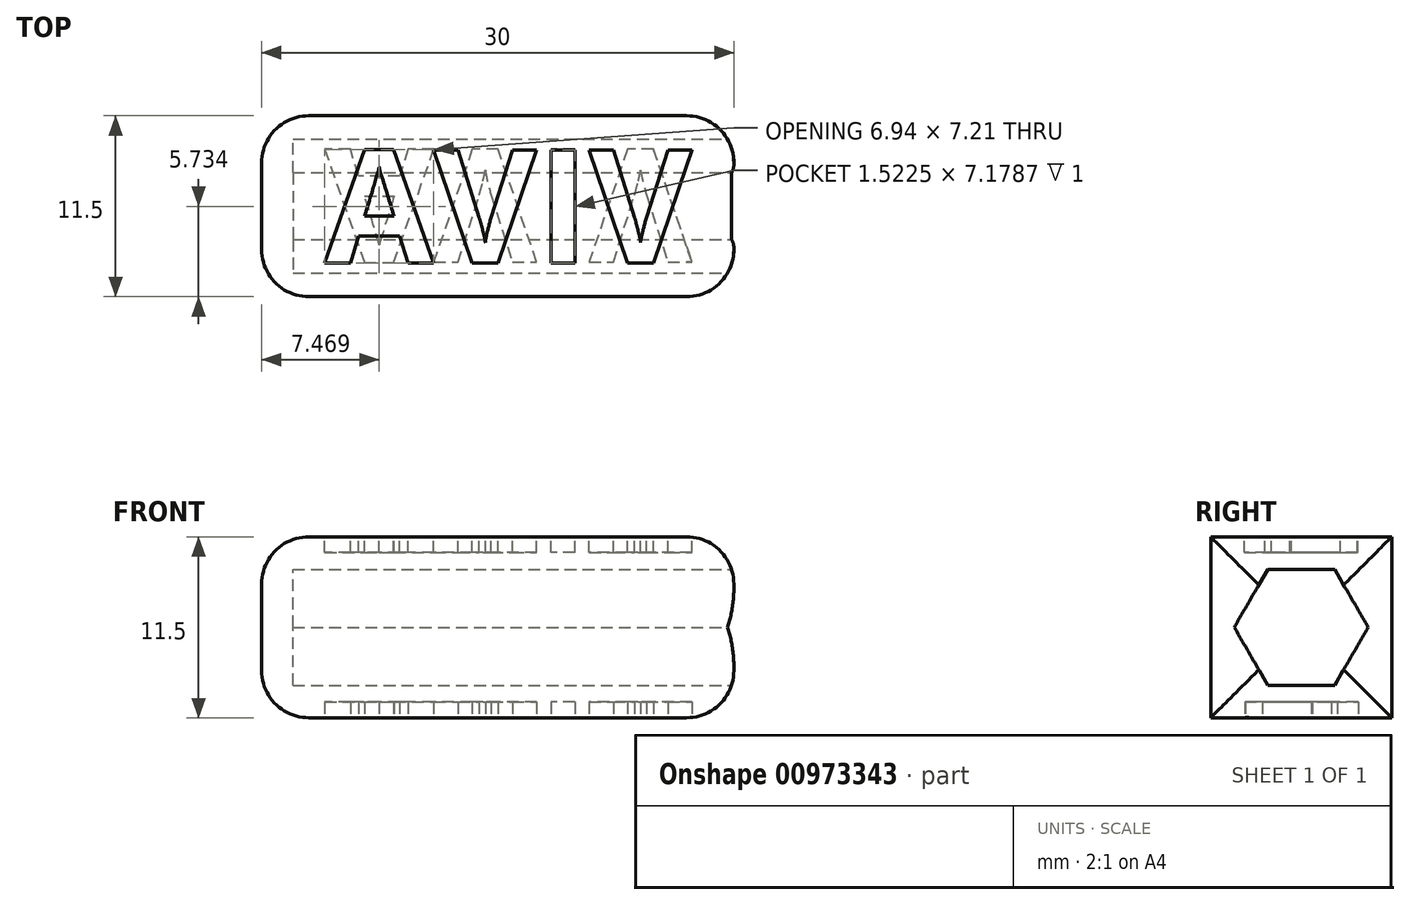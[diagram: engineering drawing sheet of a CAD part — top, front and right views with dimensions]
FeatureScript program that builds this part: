
annotation { "Feature Type Name" : "Feature", "Feature Type Description" : "" }
export const myFeature = defineFeature(function(context is Context, id is Id, definition is map)
    precondition{}
    {
        {
            var Q0;
            Q0=qCreatedBy(makeId("Top.planeOp"),FACE);
            var sketch = newSketch(context, id + "F0", { "sketchPlane" : qUnion([Q0])});
            skCircle(sketch, "E0.cCircle", {"center": v(0, 0) * mm, "radius": 4.25 * mm, "construction": true});
            skLineSegment(sketch, "E0.0", {"start": v(0, 4.25) * mm, "end": v(3.68, 2.13) * mm});
            skLineSegment(sketch, "E0.1", {"start": v(3.68, 2.13) * mm, "end": v(3.68, -2.12) * mm});
            skLineSegment(sketch, "E0.2", {"start": v(3.68, -2.12) * mm, "end": v(0, -4.25) * mm});
            skLineSegment(sketch, "E0.3", {"start": v(0, -4.25) * mm, "end": v(-3.68, -2.13) * mm});
            skLineSegment(sketch, "E0.4", {"start": v(-3.68, -2.13) * mm, "end": v(-3.68, 2.12) * mm});
            skLineSegment(sketch, "E0.5", {"start": v(-3.68, 2.12) * mm, "end": v(0, 4.25) * mm});
            skLineSegment(sketch, "E1.bottom", {"start": v(5.75, 5.75) * mm, "end": v(-5.75, 5.75) * mm});
            skLineSegment(sketch, "E1.top", {"start": v(5.75, -5.75) * mm, "end": v(-5.75, -5.75) * mm});
            skLineSegment(sketch, "E1.left", {"start": v(5.75, 5.75) * mm, "end": v(5.75, -5.75) * mm});
            skLineSegment(sketch, "E1.right", {"start": v(-5.75, 5.75) * mm, "end": v(-5.75, -5.75) * mm});
            skSolve(sketch);
        }
        {
            var Q0;
            Q0=makeQuery(id+"F0.imprint","IMPRINT",FACE,{"disambiguationData":[TD([[makeQuery(id+"F0.imprint","IMPRINT",EDGE,{"derivedFrom":sQuery(id+"F0.wireOp",EDGE,"E1.bottom")}),1.0]])]});
            var Q1;
            {var subQ0=sQuery(id+"F0.wireOp",EDGE,"E0.3");Q1=makeQuery(id+"F0.imprint","IMPRINT",FACE,{"disambiguationData":[TD([[makeQuery(id+"F0.imprint","IMPRINT",EDGE,{"derivedFrom":subQ0}),1.0]])]});}
            var Q2;
            {var subQ0=sQuery(id+"F0.wireOp",EDGE,"E0.2");Q2=makeQuery(id+"F0.imprint","IMPRINT",FACE,{"disambiguationData":[TD([[makeQuery(id+"F0.imprint","IMPRINT",EDGE,{"derivedFrom":subQ0}),1.0]])]});}
            extrude(context, id + "F1", {"entities" : qUnion([Q0, Q1, Q2]), "depth" : 28 * mm, "offsetDistance" : 25 * mm});
        }
        {
            var Q0;
            Q0=qCreatedBy(makeId("Top.planeOp"),FACE);
            var sketch = newSketch(context, id + "F2", { "sketchPlane" : qUnion([Q0])});
            skLineSegment(sketch, "E2.bottom", {"start": v(-9.81, 5.37) * mm, "end": v(-20.85, 5.37) * mm});
            skLineSegment(sketch, "E2.top", {"start": v(-9.81, -5.37) * mm, "end": v(-20.85, -5.37) * mm});
            skLineSegment(sketch, "E2.left", {"start": v(-9.81, 5.37) * mm, "end": v(-9.81, -5.37) * mm});
            skLineSegment(sketch, "E2.right", {"start": v(-20.85, 5.37) * mm, "end": v(-20.85, -5.37) * mm});
            skPoint(sketch, "E2.middle", {"position": v(-15.33, 0) * mm});
            skSolve(sketch);
        }
        {
            var Q0;
            Q0=makeQuery(id+"F1.opExtrude","SWEPT_BODY",BODY,{"disambiguationData":[OSD([sQuery(id+"F0.wireOp",EDGE,"E0.0"),sQuery(id+"F0.wireOp",EDGE,"E0.1"),sQuery(id+"F0.wireOp",EDGE,"E0.2"),sQuery(id+"F0.wireOp",EDGE,"E0.3"),sQuery(id+"F0.wireOp",EDGE,"E0.4"),sQuery(id+"F0.wireOp",EDGE,"E0.5"),sQuery(id+"F0.wireOp",EDGE,"E1.bottom"),sQuery(id+"F0.wireOp",EDGE,"E1.top"),sQuery(id+"F0.wireOp",EDGE,"E1.left"),sQuery(id+"F0.wireOp",EDGE,"E1.right")])]});
            var Q1;
            Q1=sQuery(id+"F2.wireOp",EDGE,"E2.left");
            transform(context, id + "F3", {"entities" : qUnion([Q0]), "transformType" : TransformType.ROTATION, "transformAxis" : qUnion([Q1]), "angle" : 90 * degree, "makeCopy" : false});
        }
        {
            var Q0;
            Q0=makeQuery(id+"F1.opExtrude","SWEPT_FACE",FACE,{"disambiguationData":[OSD([sQuery(id+"F0.wireOp",EDGE,"E1.right")])]});
            var sketch = newSketch(context, id + "F4", { "sketchPlane" : qUnion([Q0])});
            skPoint(sketch, "E3", {"position": v(-35.81, 3.62) * mm});
            skPoint(sketch, "E4", {"position": v(-11.81, -3.62) * mm});
            skText(sketch, "E5", { "text": "AVIV", "fontName": "OpenSans-Bold.ttf"});
            skLineSegment(sketch, "E6", {"start": v(-37.81, 5.75) * mm, "end": v(-9.81, 5.75) * mm});
            skLineSegment(sketch, "E7", {"start": v(-23.81, 5.75) * mm, "end": v(-23.81, -5.75) * mm});
            skPoint(sketch, "E8", {"position": v(-23.81, 0) * mm});
            const initialGuessF4  = {"E5": [-0.03581, -0.00362, 1, 0, 0.00724]};
            skSetInitialGuess(sketch, initialGuessF4);
            skSolve(sketch);
        }
        {
            var Q0;
            Q0=makeQuery(id+"F1.opExtrude","SWEPT_FACE",FACE,{"disambiguationData":[OSD([sQuery(id+"F0.wireOp",EDGE,"E1.left")])]});
            var sketch = newSketch(context, id + "F5", { "sketchPlane" : qUnion([Q0])});
            skPoint(sketch, "E9", {"position": v(-11.81, -3.62) * mm});
            skPoint(sketch, "E10", {"position": v(-35.81, 3.62) * mm});
            skText(sketch, "E11", { "text": "AVIV", "fontName": "OpenSans-Bold.ttf"});
            skLineSegment(sketch, "E12", {"start": v(-9.81, -5.75) * mm, "end": v(-37.81, -5.75) * mm});
            skLineSegment(sketch, "E13", {"start": v(-23.81, -5.75) * mm, "end": v(-23.81, 5.75) * mm});
            skPoint(sketch, "E14", {"position": v(-23.81, 0) * mm});
            const initialGuessF5  = {"E11": [-0.03581, -0.00362, 1, 0, 0.00724]};
            skSetInitialGuess(sketch, initialGuessF5);
            skSolve(sketch);
        }
        {
            var Q0;
            Q0 = qSketchRegion(id + "F4", true);
            extrude(context, id + "F6", {"entities" : qUnion([Q0]), "operationType" : NewBodyOperationType.REMOVE, "oppositeDirection" : true, "depth" : 1 * mm, "offsetDistance" : 25 * mm});
        }
        {
            var Q0;
            Q0=makeQuery(id+"F5.imprint","IMPRINT",FACE,{"disambiguationData":[TD([[makeQuery(id+"F5.imprint","IMPRINT",EDGE,{"derivedFrom":sQuery(id+"F5.wireOp",EDGE,"E11.sketch_text.stroke-0")}),-1.0]])]});
            var Q1;
            {var subQ6=sQuery(id+"F5.wireOp",EDGE,"E11.sketch_text.stroke-14");Q1=makeQuery(id+"F5.imprint","IMPRINT",FACE,{"disambiguationData":[TD([[makeQuery(id+"F5.imprint","IMPRINT",EDGE,{"derivedFrom":subQ6}),-1.0]])]});}
            var Q2;
            Q2=makeQuery(id+"F5.imprint","IMPRINT",FACE,{"disambiguationData":[TD([[makeQuery(id+"F5.imprint","IMPRINT",EDGE,{"derivedFrom":sQuery(id+"F5.wireOp",EDGE,"E11.sketch_text.stroke-22")}),-1.0]])]});
            var Q3;
            {var subQ0=sQuery(id+"F5.wireOp",EDGE,"E11.sketch_text.stroke-13");var subQ1=sQuery(id+"F5.wireOp",EDGE,"E11.sketch_text.stroke-12");var subQ2=makeQuery(id+"F5.imprint","INTERSECT",VERTEX,{"derivedFrom":[subQ1,subQ0]});Q3=makeQuery(id+"F5.imprint","IMPRINT",FACE,{"disambiguationData":[TD([[makeQuery(id+"F5.imprint","IMPRINT",EDGE,{"disambiguationData":[TD([[subQ2,1.0]])],"derivedFrom":subQ1}),-1.0]])]});}
            var Q4;
            Q4=makeQuery(id+"F5.imprint","IMPRINT",FACE,{"disambiguationData":[TD([[makeQuery(id+"F5.imprint","IMPRINT",EDGE,{"derivedFrom":sQuery(id+"F5.wireOp",EDGE,"E11.sketch_text.stroke-26")}),-1.0]])]});
            extrude(context, id + "F7", {"entities" : qUnion([Q0, Q1, Q2, Q3, Q4]), "operationType" : NewBodyOperationType.REMOVE, "oppositeDirection" : true, "depth" : 1 * mm, "offsetDistance" : 25 * mm});
        }
        {
            var Q0;
            Q0=makeQuery(id+"F1.opExtrude","CAP_FACE",FACE,{"disambiguationData":[OSD([sQuery(id+"F0.wireOp",EDGE,"E0.0"),sQuery(id+"F0.wireOp",EDGE,"E0.1"),sQuery(id+"F0.wireOp",EDGE,"E0.2"),sQuery(id+"F0.wireOp",EDGE,"E0.3"),sQuery(id+"F0.wireOp",EDGE,"E0.4"),sQuery(id+"F0.wireOp",EDGE,"E0.5"),sQuery(id+"F0.wireOp",EDGE,"E1.bottom"),sQuery(id+"F0.wireOp",EDGE,"E1.top"),sQuery(id+"F0.wireOp",EDGE,"E1.left"),sQuery(id+"F0.wireOp",EDGE,"E1.right")])],"isStart":false});
            var sketch = newSketch(context, id + "F8", { "sketchPlane" : qUnion([Q0])});
            skLineSegment(sketch, "E15.bottom", {"start": v(-5.75, 4.06) * mm, "end": v(5.75, 4.06) * mm});
            skLineSegment(sketch, "E15.top", {"start": v(-5.75, 15.56) * mm, "end": v(5.75, 15.56) * mm});
            skLineSegment(sketch, "E15.left", {"start": v(-5.75, 4.06) * mm, "end": v(-5.75, 15.56) * mm});
            skLineSegment(sketch, "E15.right", {"start": v(5.75, 4.06) * mm, "end": v(5.75, 15.56) * mm});
            skSolve(sketch);
        }
        {
            var Q0;
            Q0 = qSketchRegion(id + "F8", true);
            extrude(context, id + "F9", {"entities" : qUnion([Q0]), "operationType" : NewBodyOperationType.ADD, "depth" : 2 * mm, "offsetDistance" : 25 * mm, "hasDraft" : true, "draftAngle" : 3 * degree});
        }
        {
            var Q0;
            Q0=makeQuery(id+"F1.opExtrude","CAP_EDGE",EDGE,{"disambiguationData":[OSD([sQuery(id+"F0.wireOp",EDGE,"E1.right")])],"isStart":true});
            var Q1;
            Q1=makeQuery(id+"F1.opExtrude","CAP_EDGE",EDGE,{"disambiguationData":[OSD([sQuery(id+"F0.wireOp",EDGE,"E1.left")])],"isStart":true});
            var Q2;
            Q2=makeQuery(id+"F9.opExtrude","CAP_EDGE",EDGE,{"disambiguationData":[OSD([sQuery(id+"F8.wireOp",EDGE,"E15.bottom")])],"isStart":false});
            var Q3;
            Q3=makeQuery(id+"F9.opExtrude","CAP_EDGE",EDGE,{"disambiguationData":[OSD([sQuery(id+"F8.wireOp",EDGE,"E15.top")])],"isStart":false});
            var Q4;
            Q4=makeQuery(id+"F9.opExtrude","CAP_EDGE",EDGE,{"disambiguationData":[OSD([sQuery(id+"F8.wireOp",EDGE,"E15.left")])],"isStart":false});
            var Q5;
            Q5=makeQuery(id+"F9.opExtrude","CAP_EDGE",EDGE,{"disambiguationData":[OSD([sQuery(id+"F8.wireOp",EDGE,"E15.right")])],"isStart":false});
            var Q6;
            Q6=makeQuery(id+"F1.opExtrude","CAP_EDGE",EDGE,{"disambiguationData":[OSD([sQuery(id+"F0.wireOp",EDGE,"E1.bottom")])],"isStart":true});
            var Q7;
            Q7=makeQuery(id+"F1.opExtrude","CAP_EDGE",EDGE,{"disambiguationData":[OSD([sQuery(id+"F0.wireOp",EDGE,"E1.top")])],"isStart":true});
            fillet(context, id + "F10", {"entities" : qUnion([Q0, Q1, Q2, Q3, Q4, Q5, Q6, Q7]), "radius" : 3 * mm, "tangentPropagation" : true, "allowEdgeOverflow" : false});
        }
    });
